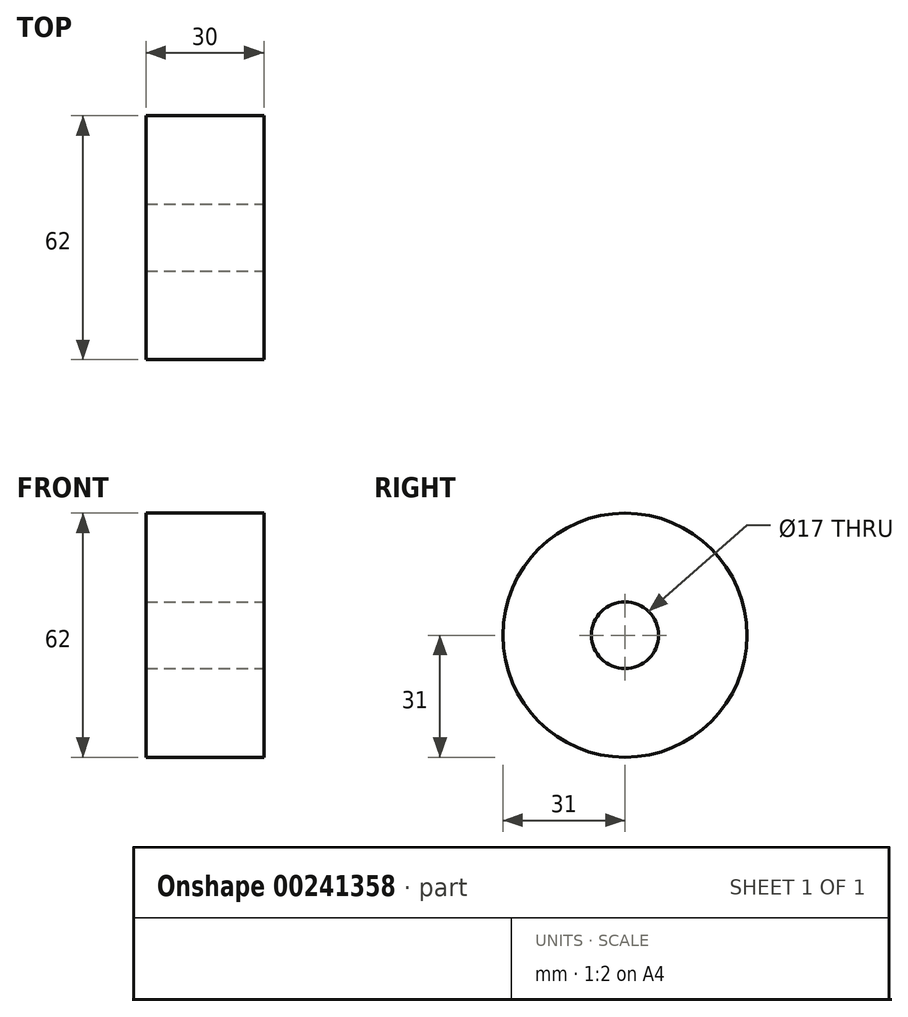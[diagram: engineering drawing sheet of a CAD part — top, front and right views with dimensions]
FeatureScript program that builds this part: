
annotation { "Feature Type Name" : "Feature", "Feature Type Description" : "" }
export const myFeature = defineFeature(function(context is Context, id is Id, definition is map)
    precondition{}
    {
        {
            var Q0;
            Q0=qCreatedBy(makeId("Right.planeOp"),FACE);
            var sketch = newSketch(context, id + "F0", { "sketchPlane" : qUnion([Q0])});
            skCircle(sketch, "E0", {"center": v(0, 0) * mm, "radius": 31 * mm});
            skSolve(sketch);
        }
        {
            var Q0;
            Q0 = qSketchRegion(id + "F0", true);
            extrude(context, id + "F1", {"entities" : qUnion([Q0]), "depth" : 30 * mm, "offsetDistance" : 25 * mm});
        }
        {
            var Q0;
            Q0=makeQuery(id+"F1.opExtrude","CAP_FACE",FACE,{"disambiguationData":[OSD([sQuery(id+"F0.wireOp",EDGE,"E0")])],"isStart":false});
            var sketch = newSketch(context, id + "F2", { "sketchPlane" : qUnion([Q0])});
            skCircle(sketch, "E1", {"center": v(0, 0) * mm, "radius": 8.5 * mm});
            skSolve(sketch);
        }
        {
            var Q0;
            Q0 = qSketchRegion(id + "F2", true);
            extrude(context, id + "F3", {"entities" : qUnion([Q0]), "operationType" : NewBodyOperationType.REMOVE, "endBound" : BoundingType.THROUGH_ALL, "oppositeDirection" : true, "depth" : 25 * mm});
        }
    });
